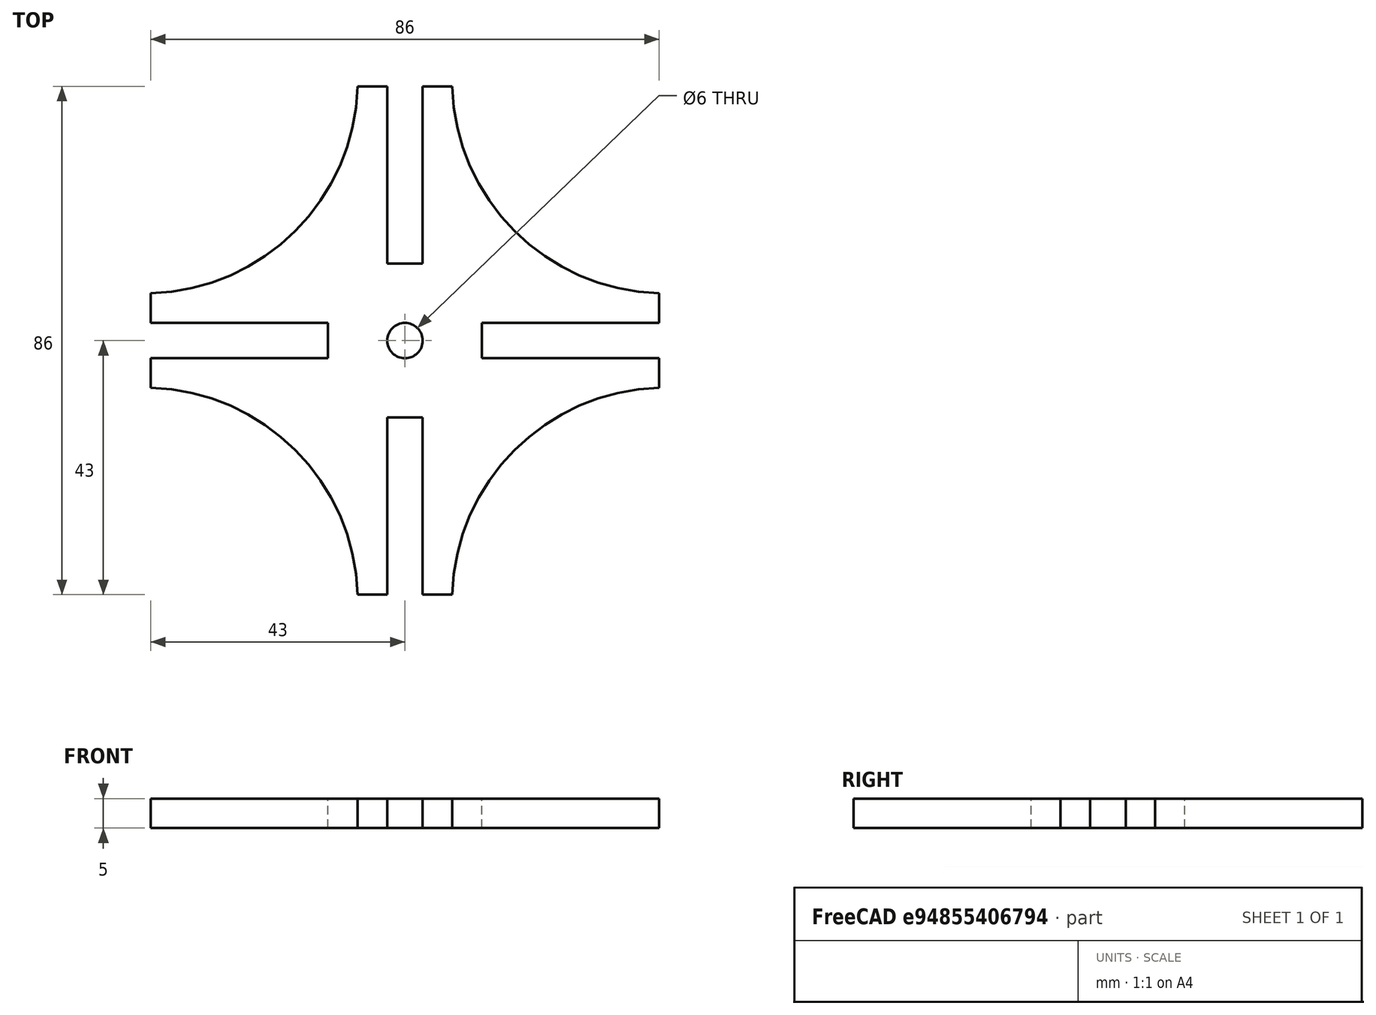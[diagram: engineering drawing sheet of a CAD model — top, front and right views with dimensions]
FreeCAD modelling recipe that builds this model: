
FCSTD DOCUMENT
Label: MalteseCross
objects: Sketcher::SketchObject×1, PartDesign::Pad×1
note: 3 computed .brp shape members not serialized (recipe doc carries the construction recipe); baked Part::Feature solids carry a one-line shape summary decoded from their .brp

FEATURE [Sketcher::SketchObject] Sketch
  sketch-geometry (45):
    g0: LineSegment StartX=3 StartY=43 StartZ=0 EndX=3 EndY=13 EndZ=0
    g1: LineSegment StartX=3 StartY=13 StartZ=0 EndX=-3 EndY=13 EndZ=0
    g2: LineSegment StartX=-3 StartY=13 StartZ=0 EndX=-3 EndY=43 EndZ=0
    g3: LineSegment StartX=-3 StartY=-13 StartZ=0 EndX=3 EndY=-13 EndZ=0
    g4: LineSegment StartX=3 StartY=-13 StartZ=0 EndX=3 EndY=-43 EndZ=0
    g5: LineSegment StartX=-3 StartY=-43 StartZ=0 EndX=-3 EndY=-13 EndZ=0
    g6: LineSegment StartX=13 StartY=3 StartZ=0 EndX=43 EndY=3 EndZ=0
    g7: LineSegment StartX=-13 StartY=3 StartZ=0 EndX=-43 EndY=3 EndZ=0
    g8: LineSegment StartX=-43 StartY=-3 StartZ=0 EndX=-13 EndY=-3 EndZ=0
    g9: LineSegment StartX=-13 StartY=-3 StartZ=0 EndX=-13 EndY=3 EndZ=0
    g10: LineSegment [constr] StartX=-3 StartY=3 StartZ=0 EndX=3 EndY=3 EndZ=0
    g11: LineSegment [constr] StartX=3 StartY=3 StartZ=0 EndX=3 EndY=-3 EndZ=0
    g12: LineSegment [constr] StartX=3 StartY=-3 StartZ=0 EndX=-3 EndY=-3 EndZ=0
    g13: LineSegment [constr] StartX=-3 StartY=-3 StartZ=0 EndX=-3 EndY=3 EndZ=0
    g14: LineSegment [constr] StartX=-3 StartY=13 StartZ=0 EndX=-3 EndY=3 EndZ=0
    g15: LineSegment [constr] StartX=3 StartY=13 StartZ=0 EndX=3 EndY=3 EndZ=0
    g16: LineSegment [constr] StartX=-3 StartY=-3 StartZ=0 EndX=-3 EndY=-13 EndZ=0
    g17: LineSegment [constr] StartX=3 StartY=-3 StartZ=0 EndX=3 EndY=-13 EndZ=0
    g18: LineSegment [constr] StartX=-3 StartY=3 StartZ=0 EndX=-13 EndY=3 EndZ=0
    g19: LineSegment [constr] StartX=-3 StartY=-3 StartZ=0 EndX=-13 EndY=-3 EndZ=0
    g20: LineSegment [constr] StartX=3 StartY=3 StartZ=0 EndX=13 EndY=3 EndZ=0
    g21: LineSegment [constr] StartX=3 StartY=-3 StartZ=0 EndX=13 EndY=-3 EndZ=0
    g22: LineSegment [constr] StartX=-3 StartY=43 StartZ=0 EndX=3 EndY=43 EndZ=0
    g23: LineSegment [constr] StartX=-3 StartY=-43 StartZ=0 EndX=3 EndY=-43 EndZ=0
    g24: LineSegment [constr] StartX=-43 StartY=3 StartZ=0 EndX=-43 EndY=-3 EndZ=0
    g25: LineSegment StartX=3 StartY=43 StartZ=0 EndX=8 EndY=43 EndZ=0
    g26: LineSegment StartX=-3 StartY=43 StartZ=0 EndX=-8 EndY=43 EndZ=0
    g27: LineSegment StartX=-43 StartY=3 StartZ=0 EndX=-43 EndY=8 EndZ=0
    g28: LineSegment StartX=-43 StartY=-3 StartZ=0 EndX=-43 EndY=-8 EndZ=0
    g29: LineSegment StartX=3 StartY=-43 StartZ=0 EndX=8 EndY=-43 EndZ=0
    g30: LineSegment [constr] StartX=3 StartY=3 StartZ=0 EndX=0 EndY=0 EndZ=0
    g31: LineSegment [constr] StartX=-3 StartY=3 StartZ=0 EndX=0 EndY=0 EndZ=0
    g32: LineSegment [constr] StartX=3 StartY=-3 StartZ=0 EndX=0 EndY=0 EndZ=0
    g33: LineSegment [constr] StartX=0 StartY=0 StartZ=0 EndX=-3 EndY=-3 EndZ=0
    g34: Circle CenterX=0 CenterY=0 CenterZ=0 NormalX=0 NormalY=0 NormalZ=1 Radius=3
    g35: LineSegment [constr] StartX=43 StartY=-3 StartZ=0 EndX=43 EndY=3 EndZ=0
    g36: LineSegment StartX=43 StartY=3 StartZ=0 EndX=43 EndY=8 EndZ=0
    g37: LineSegment StartX=43 StartY=-3 StartZ=0 EndX=43 EndY=-8 EndZ=0
    g38: LineSegment StartX=-3 StartY=-43 StartZ=0 EndX=-8 EndY=-43 EndZ=0
    g39: LineSegment StartX=13 StartY=-3 StartZ=0 EndX=43 EndY=-3 EndZ=0
    g40: LineSegment StartX=13 StartY=3 StartZ=0 EndX=13 EndY=-3 EndZ=0
    g41: ArcOfCircle CenterX=-43.9865 CenterY=43.9865 CenterZ=0 NormalX=0 NormalY=0 NormalZ=1 Radius=36 StartAngle=4.73979 EndAngle=6.25578
    g42: ArcOfCircle CenterX=-43.9865 CenterY=-43.9865 CenterZ=0 NormalX=0 NormalY=0 NormalZ=1 Radius=36 StartAngle=0.0274057 EndAngle=1.54339
    g43: ArcOfCircle CenterX=43.9865 CenterY=-43.9865 CenterZ=0 NormalX=0 NormalY=0 NormalZ=1 Radius=36 StartAngle=1.5982 EndAngle=3.11419
    g44: ArcOfCircle CenterX=43.9865 CenterY=43.9865 CenterZ=0 NormalX=0 NormalY=0 NormalZ=1 Radius=36 StartAngle=3.169 EndAngle=4.68498
  constraints (123):
    c: Coincident(g0,g1)
    c: Coincident(g1,g2)
    c: Horizontal(g1)
    c: Vertical(g0)
    c: Vertical(g2)
    c: Coincident(g3,g4)
    c: Coincident(g5,g3)
    c: Horizontal(g3)
    c: Vertical(g4)
    c: Vertical(g5)
    c: Horizontal(g6)
    c: Coincident(g8,g9)
    c: Coincident(g9,g7)
    c: Horizontal(g7)
    c: Horizontal(g8)
    c: Vertical(g9)
    c: Coincident(g10,g11)
    c: Coincident(g11,g12)
    c: Coincident(g12,g13)
    c: Coincident(g13,g10)
    c: Horizontal(g10)
    c: Horizontal(g12)
    c: Vertical(g11)
    c: Vertical(g13)
    c: Vertical(g14)
    c: Vertical(g15)
    c: Coincident(g10,g14)
    c: Coincident(g14,g1)
    c: Coincident(g15,g0)
    c: Coincident(g15,g10)
    c: Vertical(g16)
    c: Vertical(g17)
    c: Coincident(g17,g3)
    c: Coincident(g11,g17)
    c: Coincident(g3,g16)
    c: Coincident(g16,g12)
    c: Horizontal(g18)
    c: Horizontal(g19)
    c: Coincident(g12,g19)
    c: Coincident(g10,g18)
    c: Coincident(g7,g18)
    c: Coincident(g19,g8)
    c: Horizontal(g20)
    c: Horizontal(g21)
    c: Coincident(g6,g20)
    c: Coincident(g20,g10)
    c: Coincident(g21,g11)
    c: Horizontal(g22)
    c: Coincident(g2,g22)
    c: Horizontal(g23)
    c: Coincident(g23,g4)
    c: Coincident(g23,g5)
    c: Vertical(g24)
    c: Coincident(g8,g24)
    c: Coincident(g24,g7)
    c: Coincident(g22,g0)
    c: Equal(g1,g9)
    c: DistanceY(g7,g8) = -6
    c: Equal(g14,g18)
    c: Equal(g16,g19)
    c: Equal(g20,g15)
    c: Horizontal(g25)
    c: Coincident(g25,g0)
    c: Horizontal(g26)
    c: Vertical(g27)
    c: Coincident(g2,g26)
    c: Coincident(g7,g27)
    c: Equal(g27,g26)
    c: Vertical(g28)
    c: Coincident(g28,g8)
    c: Horizontal(g29)
    c: Coincident(g29,g4)
    c: Equal(g2,g7)
    c: Equal(g6,g0)
    c: Equal(g25,g26)
    c: DistanceY(g27) = 5
    c: DistanceX(g8) = 30
    c: DistanceX(g19) = -10
    c: Coincident(g30,g31)
    c: Coincident(g33,g32)
    c: Coincident(g32,g30)
    c: Coincident(g33,g12)
    c: Coincident(g31,g10)
    c: Coincident(g32,g11)
    c: Coincident(g30,g10)
    c: Equal(g30,g33)
    c: Parallel(g33,g30)
    c: Coincident(g34,g30)
    c: Radius(g34) = 3
    c: DistanceX(g30) = 0
    c: DistanceY(g30) = 0
    c: Vertical(g35)
    c: Coincident(g6,g35)
    c: Vertical(g36)
    c: Vertical(g37)
    c: Horizontal(g38)
    c: Coincident(g37,g35)
    c: Coincident(g36,g6)
    c: Horizontal(g39)
    c: Coincident(g39,g21)
    c: Vertical(g40)
    c: Coincident(g40,g21)
    c: Coincident(g40,g6)
    c: Coincident(g39,g35)
    c: Equal(g29,g38)
    c: Equal(g37,g36)
    c: Equal(g36,g25)
    c: Coincident(g5,g38)
    c: Equal(g5,g8)
    c: Equal(g28,g27)
    c: Equal(g37,g29)
    c: Coincident(g26,g41)
    c: Coincident(g27,g41)
    c: Coincident(g44,g25)
    c: Coincident(g44,g36)
    c: Coincident(g43,g37)
    c: Coincident(g43,g29)
    c: Coincident(g42,g38)
    c: Coincident(g42,g28)
    c: Radius(g41) = 36
    c: Equal(g44,g41)
    c: Equal(g41,g42)
    c: Equal(g41,g43)
FEATURE [PartDesign::Pad] Pad
  Length = 5
  MirroredExtent = false
  Sketch = -> Sketch
